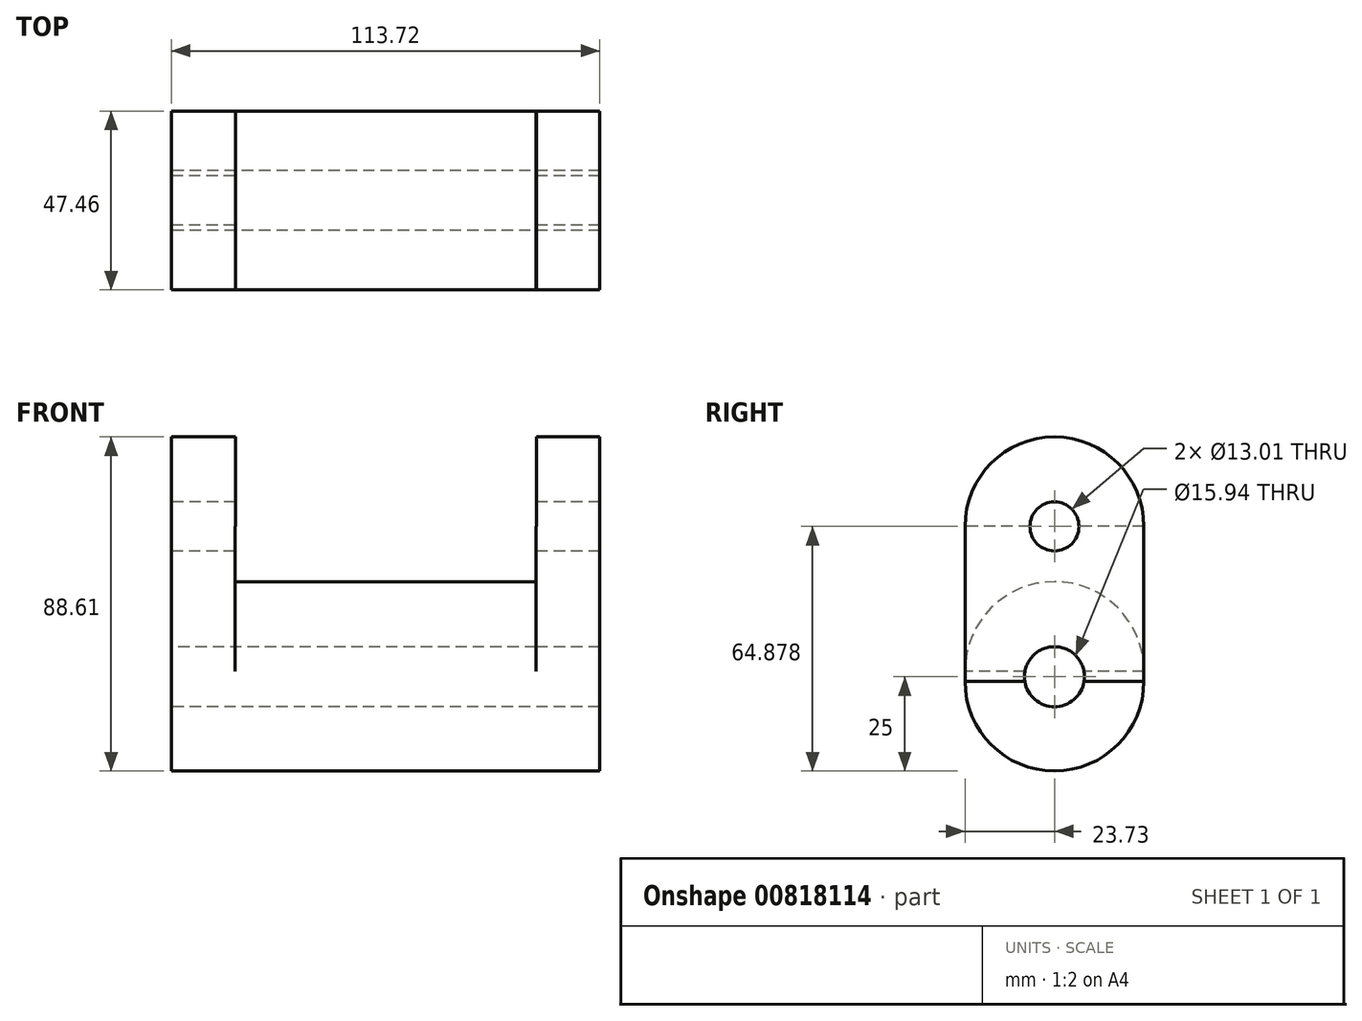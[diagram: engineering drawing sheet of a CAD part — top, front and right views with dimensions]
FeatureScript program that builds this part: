
annotation { "Feature Type Name" : "Feature", "Feature Type Description" : "" }
export const myFeature = defineFeature(function(context is Context, id is Id, definition is map)
    precondition{}
    {
        {
            var Q0;
            Q0=qCreatedBy(makeId("Top.planeOp"),FACE);
            var sketch = newSketch(context, id + "F0", { "sketchPlane" : qUnion([Q0])});
            skLineSegment(sketch, "E0.bottom", {"start": v(39.5, 23.73) * mm, "end": v(-39.5, 23.73) * mm});
            skLineSegment(sketch, "E0.top", {"start": v(39.5, -23.73) * mm, "end": v(-39.5, -23.73) * mm});
            skLineSegment(sketch, "E0.left", {"start": v(39.5, 23.73) * mm, "end": v(39.5, -23.73) * mm});
            skLineSegment(sketch, "E0.right", {"start": v(-39.5, 23.73) * mm, "end": v(-39.5, -23.73) * mm});
            skPoint(sketch, "E0.middle", {"position": v(0, 0) * mm});
            skLineSegment(sketch, "E1.bottom", {"start": v(-39.5, 0) * mm, "end": v(-56.86, 0) * mm});
            skLineSegment(sketch, "E1.top", {"start": v(-39.5, 23.73) * mm, "end": v(-56.86, 23.73) * mm});
            skLineSegment(sketch, "E1.left", {"start": v(-39.5, 0) * mm, "end": v(-39.5, 23.73) * mm});
            skLineSegment(sketch, "E1.right", {"start": v(-56.86, 0) * mm, "end": v(-56.86, 23.73) * mm});
            skLineSegment(sketch, "E2.bottom", {"start": v(-56.86, 0) * mm, "end": v(-39.5, 0) * mm});
            skLineSegment(sketch, "E2.top", {"start": v(-56.86, -23.73) * mm, "end": v(-39.5, -23.73) * mm});
            skLineSegment(sketch, "E2.left", {"start": v(-56.86, 0) * mm, "end": v(-56.86, -23.73) * mm});
            skLineSegment(sketch, "E2.right", {"start": v(-39.5, 0) * mm, "end": v(-39.5, -23.73) * mm});
            skLineSegment(sketch, "E3.bottom", {"start": v(39.5, 23.73) * mm, "end": v(56.86, 23.73) * mm});
            skLineSegment(sketch, "E3.top", {"start": v(39.5, 0) * mm, "end": v(56.86, 0) * mm});
            skLineSegment(sketch, "E3.left", {"start": v(39.5, 23.73) * mm, "end": v(39.5, 0) * mm});
            skLineSegment(sketch, "E3.right", {"start": v(56.86, 23.73) * mm, "end": v(56.86, 0) * mm});
            skLineSegment(sketch, "E4.bottom", {"start": v(56.86, 0) * mm, "end": v(39.5, 0) * mm});
            skLineSegment(sketch, "E4.top", {"start": v(56.86, -23.73) * mm, "end": v(39.5, -23.73) * mm});
            skLineSegment(sketch, "E4.left", {"start": v(56.86, 0) * mm, "end": v(56.86, -23.73) * mm});
            skLineSegment(sketch, "E4.right", {"start": v(39.5, 0) * mm, "end": v(39.5, -23.73) * mm});
            skSolve(sketch);
        }
        {
            var Q0;
            {var subQ2=sQuery(id+"F0.wireOp",EDGE,"E1.bottom");Q0=makeQuery(id+"F0.imprint","IMPRINT",FACE,{"disambiguationData":[TD([[makeQuery(id+"F0.imprint","IMPRINT",EDGE,{"derivedFrom":subQ2}),-1.0]])]});}
            var Q1;
            {var subQ2=sQuery(id+"F0.wireOp",EDGE,"E1.bottom");Q1=makeQuery(id+"F0.imprint","IMPRINT",FACE,{"disambiguationData":[TD([[makeQuery(id+"F0.imprint","IMPRINT",EDGE,{"derivedFrom":subQ2}),1.0]])]});}
            var Q2;
            {var subQ1=sQuery(id+"F0.wireOp",EDGE,"E0.bottom");Q2=makeQuery(id+"F0.imprint","IMPRINT",FACE,{"disambiguationData":[TD([[makeQuery(id+"F0.imprint","IMPRINT",EDGE,{"derivedFrom":subQ1}),1.0]])]});}
            var Q3;
            {var subQ0=sQuery(id+"F0.wireOp",EDGE,"E3.bottom");Q3=makeQuery(id+"F0.imprint","IMPRINT",FACE,{"disambiguationData":[TD([[makeQuery(id+"F0.imprint","IMPRINT",EDGE,{"derivedFrom":subQ0}),-1.0]])]});}
            var Q4;
            {var subQ2=sQuery(id+"F0.wireOp",EDGE,"E3.top");Q4=makeQuery(id+"F0.imprint","IMPRINT",FACE,{"disambiguationData":[TD([[makeQuery(id+"F0.imprint","IMPRINT",EDGE,{"derivedFrom":subQ2}),-1.0]])]});}
            extrude(context, id + "F1", {"entities" : qUnion([Q0, Q1, Q2, Q3, Q4]), "oppositeDirection" : true, "depth" : 1.27 * mm, "offsetDistance" : 25.4 * mm});
        }
        {
            var Q0;
            Q0=makeQuery(id+"F1.opExtrude","SWEPT_FACE",FACE,{"disambiguationData":[OSD([sQuery(id+"F0.wireOp",EDGE,"E1.right"),sQuery(id+"F0.wireOp",EDGE,"E2.left")])]});
            var sketch = newSketch(context, id + "F2", { "sketchPlane" : qUnion([Q0])});
            skArc(sketch, "E5", {"start": v(-23.73, -1.27) * mm, "mid": v(0, -25) * mm, "end": v(23.73, -1.27) * mm});
            skSolve(sketch);
        }
        {
            var Q0;
            Q0=qSketchRegion(id+"F2",true);
            var Q1;
            Q1=makeQuery(id+"F2.imprint","IMPRINT",FACE,{"disambiguationData":[TD([[makeQuery(id+"F2.imprint","IMPRINT",EDGE,{"derivedFrom":sQuery(id+"F2.wireOp",EDGE,"E5")}),1.0]])]});
            extrude(context, id + "F3", {"entities" : qUnion([Q0, Q1]), "operationType" : NewBodyOperationType.ADD, "oppositeDirection" : true, "depth" : 113.7 * mm, "offsetDistance" : 25.4 * mm});
        }
        {
            var Q0;
            Q0=makeQuery(id+"F1.opExtrude","CAP_FACE",FACE,{"disambiguationData":[OSD([sQuery(id+"F0.wireOp",EDGE,"E0.bottom"),sQuery(id+"F0.wireOp",EDGE,"E0.top"),sQuery(id+"F0.wireOp",EDGE,"E1.top"),sQuery(id+"F0.wireOp",EDGE,"E1.right"),sQuery(id+"F0.wireOp",EDGE,"E2.top"),sQuery(id+"F0.wireOp",EDGE,"E2.left"),sQuery(id+"F0.wireOp",EDGE,"E3.bottom"),sQuery(id+"F0.wireOp",EDGE,"E3.right"),sQuery(id+"F0.wireOp",EDGE,"E4.top"),sQuery(id+"F0.wireOp",EDGE,"E4.left")])],"isStart":true});
            var sketch = newSketch(context, id + "F4", { "sketchPlane" : qUnion([Q0])});
            skLineSegment(sketch, "E6.bottom", {"start": v(39.97, 23.73) * mm, "end": v(-39.97, 23.73) * mm});
            skLineSegment(sketch, "E6.top", {"start": v(39.97, -23.73) * mm, "end": v(-39.97, -23.73) * mm});
            skLineSegment(sketch, "E6.left", {"start": v(39.97, 23.73) * mm, "end": v(39.97, -23.73) * mm});
            skLineSegment(sketch, "E6.right", {"start": v(-39.97, 23.73) * mm, "end": v(-39.97, -23.73) * mm});
            skPoint(sketch, "E6.middle", {"position": v(0, 0) * mm});
            skSolve(sketch);
        }
        {
            var Q0;
            Q0=makeQuery(id+"F4.imprint","IMPRINT",FACE,{"disambiguationData":[TD([[makeQuery(id+"F4.imprint","IMPRINT",EDGE,{"derivedFrom":sQuery(id+"F4.wireOp",EDGE,"E6.bottom")}),1.0]])]});
            extrude(context, id + "F5", {"entities" : qUnion([Q0]), "operationType" : NewBodyOperationType.ADD, "depth" : 1.5 * mm, "offsetDistance" : 25.4 * mm});
        }
        {
            var Q0;
            Q0=makeQuery(id+"F5.opExtrude","SWEPT_FACE",FACE,{"disambiguationData":[OSD([sQuery(id+"F4.wireOp",EDGE,"E6.right")])]});
            var sketch = newSketch(context, id + "F6", { "sketchPlane" : qUnion([Q0])});
            skArc(sketch, "E7", {"start": v(23.73, 1.5) * mm, "mid": v(0, 25.23) * mm, "end": v(-23.73, 1.5) * mm});
            skSolve(sketch);
        }
        {
            var Q0;
            Q0=qSketchRegion(id+"F6",true);
            var Q1;
            Q1=makeQuery(id+"F6.imprint","IMPRINT",FACE,{"disambiguationData":[TD([[makeQuery(id+"F6.imprint","IMPRINT",EDGE,{"derivedFrom":sQuery(id+"F6.wireOp",EDGE,"E7")}),1.0]])]});
            extrude(context, id + "F7", {"entities" : qUnion([Q0, Q1]), "operationType" : NewBodyOperationType.ADD, "oppositeDirection" : true, "depth" : 79.93 * mm, "offsetDistance" : 25.4 * mm});
        }
        {
            var Q0;
            {var subQ0=sQuery(id+"F0.wireOp",EDGE,"E2.left");var subQ1=sQuery(id+"F0.wireOp",EDGE,"E1.right");var subQ2=sQuery(id+"F0.wireOp",EDGE,"E3.bottom");var subQ3=sQuery(id+"F0.wireOp",EDGE,"E1.top");var subQ4=sQuery(id+"F0.wireOp",EDGE,"E0.bottom");var subQ5=sQuery(id+"F0.wireOp",EDGE,"E4.top");var subQ6=sQuery(id+"F0.wireOp",EDGE,"E2.top");var subQ7=sQuery(id+"F0.wireOp",EDGE,"E0.top");Q0=makeQuery(id+"F5.boolean.opBoolean","SPLIT",FACE,{"disambiguationData":[TD([makeQuery(id+"F5.opExtrude","SWEPT_FACE",FACE,{"disambiguationData":[OSD([sQuery(id+"F4.wireOp",EDGE,"E6.right")])]})])],"derivedFrom":makeQuery(id+"F1.opExtrude","CAP_FACE",FACE,{"disambiguationData":[OSD([subQ4,subQ7,subQ3,subQ1,subQ6,subQ0,subQ2,sQuery(id+"F0.wireOp",EDGE,"E3.right"),subQ5,sQuery(id+"F0.wireOp",EDGE,"E4.left")])],"isStart":true})});}
            var Q1;
            {var subQ0=sQuery(id+"F0.wireOp",EDGE,"E4.left");var subQ1=sQuery(id+"F0.wireOp",EDGE,"E3.right");var subQ2=sQuery(id+"F0.wireOp",EDGE,"E4.top");var subQ3=sQuery(id+"F0.wireOp",EDGE,"E2.top");var subQ4=sQuery(id+"F0.wireOp",EDGE,"E0.top");var subQ5=sQuery(id+"F0.wireOp",EDGE,"E3.bottom");var subQ6=sQuery(id+"F0.wireOp",EDGE,"E1.top");var subQ7=sQuery(id+"F0.wireOp",EDGE,"E0.bottom");Q1=makeQuery(id+"F5.boolean.opBoolean","SPLIT",FACE,{"disambiguationData":[TD([makeQuery(id+"F5.opExtrude","SWEPT_FACE",FACE,{"disambiguationData":[OSD([sQuery(id+"F4.wireOp",EDGE,"E6.left")])]})])],"derivedFrom":makeQuery(id+"F1.opExtrude","CAP_FACE",FACE,{"disambiguationData":[OSD([subQ7,subQ4,subQ6,sQuery(id+"F0.wireOp",EDGE,"E1.right"),subQ3,sQuery(id+"F0.wireOp",EDGE,"E2.left"),subQ5,subQ1,subQ2,subQ0])],"isStart":true})});}
            extrude(context, id + "F8", {"entities" : qUnion([Q0, Q1]), "operationType" : NewBodyOperationType.ADD, "depth" : 39.88 * mm, "offsetDistance" : 25.4 * mm});
        }
        {
            var Q0;
            {var subQ0=sQuery(id+"F0.wireOp",EDGE,"E2.left");var subQ1=sQuery(id+"F0.wireOp",EDGE,"E1.right");Q0=makeQuery(id+"F8.boolean.opBoolean","MERGE",FACE,{"derivedFrom":[makeQuery(id+"F3.boolean.opBoolean","MERGE",FACE,{"derivedFrom":[makeQuery(id+"F1.opExtrude","SWEPT_FACE",FACE,{"disambiguationData":[OSD([subQ1,subQ0])]}),makeQuery(id+"F3.opExtrude","CAP_FACE",FACE,{"disambiguationData":[OSD([subQ1,subQ0,sQuery(id+"F2.wireOp",EDGE,"E5")])],"isStart":true})]}),makeQuery(id+"F8.opExtrude","SWEPT_FACE",FACE,{"disambiguationData":[OSD([subQ1,subQ0])]})]});}
            var sketch = newSketch(context, id + "F9", { "sketchPlane" : qUnion([Q0])});
            skArc(sketch, "E8", {"start": v(23.73, 39.88) * mm, "mid": v(0, 63.6) * mm, "end": v(-23.73, 39.88) * mm});
            skSolve(sketch);
        }
        {
            var Q0;
            Q0=makeQuery(id+"F9.imprint","IMPRINT",FACE,{"disambiguationData":[TD([[makeQuery(id+"F9.imprint","IMPRINT",EDGE,{"derivedFrom":sQuery(id+"F9.wireOp",EDGE,"E8")}),1.0]])]});
            extrude(context, id + "F10", {"entities" : qUnion([Q0]), "operationType" : NewBodyOperationType.ADD, "oppositeDirection" : true, "depth" : 17.02 * mm, "offsetDistance" : 25.4 * mm});
        }
        {
            var Q0;
            {var subQ0=sQuery(id+"F0.wireOp",EDGE,"E4.left");var subQ1=sQuery(id+"F0.wireOp",EDGE,"E3.right");Q0=makeQuery(id+"F8.boolean.opBoolean","MERGE",FACE,{"derivedFrom":[makeQuery(id+"F1.opExtrude","SWEPT_FACE",FACE,{"disambiguationData":[OSD([subQ1,subQ0])]}),makeQuery(id+"F8.opExtrude","SWEPT_FACE",FACE,{"disambiguationData":[OSD([subQ1,subQ0])]})]});}
            var sketch = newSketch(context, id + "F11", { "sketchPlane" : qUnion([Q0])});
            skArc(sketch, "E9", {"start": v(23.73, 39.88) * mm, "mid": v(0, 63.6) * mm, "end": v(-23.73, 39.88) * mm});
            skSolve(sketch);
        }
        {
            var Q0;
            Q0=qSketchRegion(id+"F11",true);
            var Q1;
            Q1=makeQuery(id+"F11.imprint","IMPRINT",FACE,{"disambiguationData":[TD([[makeQuery(id+"F11.imprint","IMPRINT",EDGE,{"derivedFrom":sQuery(id+"F11.wireOp",EDGE,"E9")}),1.0]])]});
            extrude(context, id + "F12", {"entities" : qUnion([Q0, Q1]), "operationType" : NewBodyOperationType.ADD, "oppositeDirection" : true, "depth" : 16.84 * mm, "offsetDistance" : 25.4 * mm});
        }
        {
            var Q0;
            {var subQ0=sQuery(id+"F0.wireOp",EDGE,"E2.left");var subQ1=sQuery(id+"F0.wireOp",EDGE,"E1.right");Q0=makeQuery(id+"F10.boolean.opBoolean","MERGE",FACE,{"derivedFrom":[makeQuery(id+"F8.boolean.opBoolean","MERGE",FACE,{"derivedFrom":[makeQuery(id+"F3.boolean.opBoolean","MERGE",FACE,{"derivedFrom":[makeQuery(id+"F1.opExtrude","SWEPT_FACE",FACE,{"disambiguationData":[OSD([subQ1,subQ0])]}),makeQuery(id+"F3.opExtrude","CAP_FACE",FACE,{"disambiguationData":[OSD([subQ1,subQ0,sQuery(id+"F2.wireOp",EDGE,"E5")])],"isStart":true})]}),makeQuery(id+"F8.opExtrude","SWEPT_FACE",FACE,{"disambiguationData":[OSD([subQ1,subQ0])]})]}),makeQuery(id+"F10.opExtrude","CAP_FACE",FACE,{"disambiguationData":[OSD([subQ1,subQ0,sQuery(id+"F9.wireOp",EDGE,"E8")])],"isStart":true})]});}
            var sketch = newSketch(context, id + "F13", { "sketchPlane" : qUnion([Q0])});
            skCircle(sketch, "E10", {"center": v(0, 39.88) * mm, "radius": 6.5 * mm});
            skSolve(sketch);
        }
        {
            var Q0;
            Q0=qSketchRegion(id+"F13",true);
            extrude(context, id + "F14", {"entities" : qUnion([Q0]), "operationType" : NewBodyOperationType.REMOVE, "oppositeDirection" : true, "depth" : 198.63 * mm, "offsetDistance" : 25.4 * mm});
        }
        {
            var Q0;
            {var subQ0=sQuery(id+"F0.wireOp",EDGE,"E2.left");var subQ1=sQuery(id+"F0.wireOp",EDGE,"E1.right");Q0=makeQuery(id+"F10.boolean.opBoolean","MERGE",FACE,{"derivedFrom":[makeQuery(id+"F8.boolean.opBoolean","MERGE",FACE,{"derivedFrom":[makeQuery(id+"F3.boolean.opBoolean","MERGE",FACE,{"derivedFrom":[makeQuery(id+"F1.opExtrude","SWEPT_FACE",FACE,{"disambiguationData":[OSD([subQ1,subQ0])]}),makeQuery(id+"F3.opExtrude","CAP_FACE",FACE,{"disambiguationData":[OSD([subQ1,subQ0,sQuery(id+"F2.wireOp",EDGE,"E5")])],"isStart":true})]}),makeQuery(id+"F8.opExtrude","SWEPT_FACE",FACE,{"disambiguationData":[OSD([subQ1,subQ0])]})]}),makeQuery(id+"F10.opExtrude","CAP_FACE",FACE,{"disambiguationData":[OSD([subQ1,subQ0,sQuery(id+"F9.wireOp",EDGE,"E8")])],"isStart":true})]});}
            var sketch = newSketch(context, id + "F15", { "sketchPlane" : qUnion([Q0])});
            skCircle(sketch, "E11", {"center": v(0, 0) * mm, "radius": 7.97 * mm});
            skSolve(sketch);
        }
        {
            var Q0;
            Q0=makeQuery(id+"F15.imprint","IMPRINT",FACE,{"disambiguationData":[TD([[makeQuery(id+"F15.imprint","IMPRINT",EDGE,{"derivedFrom":sQuery(id+"F15.wireOp",EDGE,"E11")}),1.0]])]});
            extrude(context, id + "F16", {"entities" : qUnion([Q0]), "operationType" : NewBodyOperationType.REMOVE, "oppositeDirection" : true, "depth" : 343.92 * mm, "offsetDistance" : 25.4 * mm});
        }
    });
